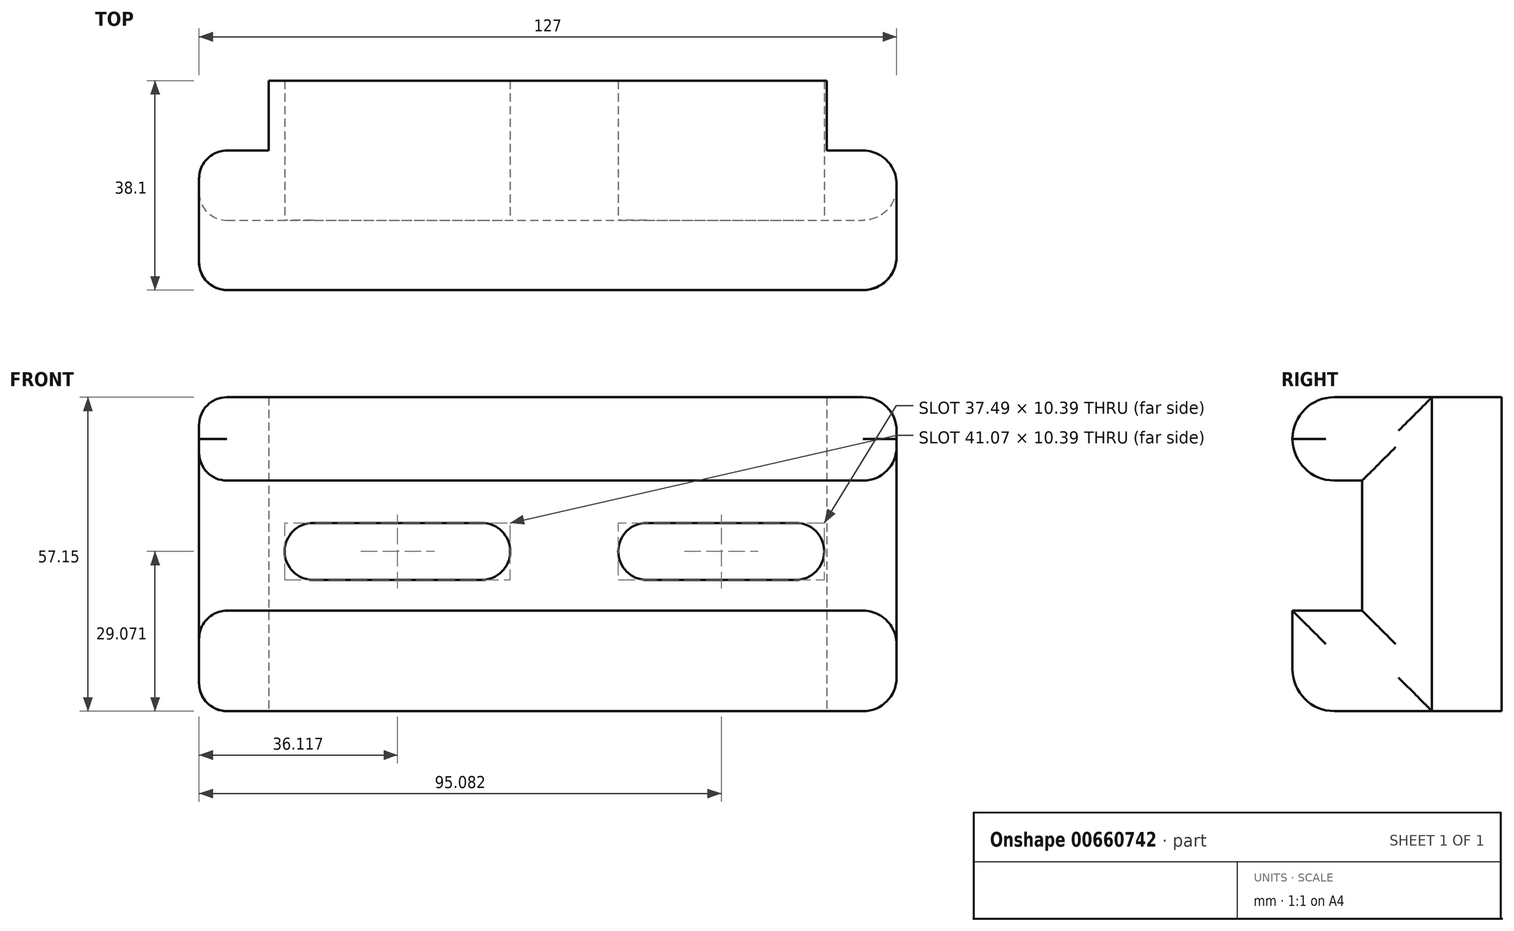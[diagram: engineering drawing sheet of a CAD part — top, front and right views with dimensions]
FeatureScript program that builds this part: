
annotation { "Feature Type Name" : "Feature", "Feature Type Description" : "" }
export const myFeature = defineFeature(function(context is Context, id is Id, definition is map)
    precondition{}
    {
        {
            var Q0;
            Q0=qCreatedBy(makeId("Front.planeOp"),FACE);
            var sketch = newSketch(context, id + "F0", { "sketchPlane" : qUnion([Q0])});
            skLineSegment(sketch, "E0", {"start": v(-81.53, -18.29) * mm, "end": v(45.47, -18.29) * mm});
            skLineSegment(sketch, "E1", {"start": v(-81.53, -18.29) * mm, "end": v(-81.53, 38.86) * mm});
            skLineSegment(sketch, "E2", {"start": v(45.47, -18.29) * mm, "end": v(45.47, 38.86) * mm});
            skLineSegment(sketch, "E3", {"start": v(45.47, 38.86) * mm, "end": v(-81.53, 38.86) * mm});
            skSolve(sketch);
        }
        {
            var Q0;
            Q0=makeQuery(id+"F0.imprint","IMPRINT",FACE,{"disambiguationData":[TD([[makeQuery(id+"F0.imprint","IMPRINT",EDGE,{"derivedFrom":sQuery(id+"F0.wireOp",EDGE,"E0")}),1.0]])]});
            extrude(context, id + "F1", {"entities" : qUnion([Q0]), "depth" : 38.1 * mm, "offsetDistance" : 25.4 * mm});
        }
        {
            var Q0;
            Q0=makeQuery(id+"F1.opExtrude","SWEPT_FACE",FACE,{"disambiguationData":[OSD([sQuery(id+"F0.wireOp",EDGE,"E0")])]});
            var sketch = newSketch(context, id + "F2", { "sketchPlane" : qUnion([Q0])});
            skLineSegment(sketch, "E4", {"start": v(45.47, 12.7) * mm, "end": v(32.77, 12.7) * mm});
            skLineSegment(sketch, "E5", {"start": v(32.77, 12.7) * mm, "end": v(32.77, 0) * mm});
            skLineSegment(sketch, "E6", {"start": v(-81.53, 12.7) * mm, "end": v(-68.83, 12.7) * mm});
            skLineSegment(sketch, "E7", {"start": v(-68.83, 12.7) * mm, "end": v(-68.83, 0) * mm});
            skSolve(sketch);
        }
        {
            var Q0;
            {var subQ0=sQuery(id+"F2.wireOp",EDGE,"E4");Q0=makeQuery(id+"F2.imprint","IMPRINT",FACE,{"disambiguationData":[TD([[makeQuery(id+"F2.imprint","IMPRINT",EDGE,{"derivedFrom":subQ0}),1.0]])]});}
            extrude(context, id + "F3", {"entities" : qUnion([Q0]), "operationType" : NewBodyOperationType.REMOVE, "oppositeDirection" : true, "depth" : 57.15 * mm, "offsetDistance" : 25.4 * mm});
        }
        {
            var Q0;
            {var subQ0=sQuery(id+"F2.wireOp",EDGE,"E6");Q0=makeQuery(id+"F2.imprint","IMPRINT",FACE,{"disambiguationData":[TD([[makeQuery(id+"F2.imprint","IMPRINT",EDGE,{"derivedFrom":subQ0}),-1.0]])]});}
            extrude(context, id + "F4", {"entities" : qUnion([Q0]), "operationType" : NewBodyOperationType.REMOVE, "oppositeDirection" : true, "depth" : 57.15 * mm, "offsetDistance" : 25.4 * mm});
        }
        {
            var Q0;
            Q0=makeQuery(id+"F1.opExtrude","CAP_FACE",FACE,{"disambiguationData":[OSD([sQuery(id+"F0.wireOp",EDGE,"E0"),sQuery(id+"F0.wireOp",EDGE,"E1"),sQuery(id+"F0.wireOp",EDGE,"E2"),sQuery(id+"F0.wireOp",EDGE,"E3")])],"isStart":false});
            var sketch = newSketch(context, id + "F5", { "sketchPlane" : qUnion([Q0])});
            skLineSegment(sketch, "E8", {"start": v(-81.53, 0) * mm, "end": v(45.47, 0) * mm});
            skLineSegment(sketch, "E9", {"start": v(-81.53, 23.68) * mm, "end": v(45.47, 23.68) * mm});
            skSolve(sketch);
        }
        {
            var Q0;
            {var subQ0=sQuery(id+"F5.wireOp",EDGE,"E8");Q0=makeQuery(id+"F5.imprint","IMPRINT",FACE,{"disambiguationData":[TD([[makeQuery(id+"F5.imprint","IMPRINT",EDGE,{"derivedFrom":subQ0}),1.0]])]});}
            extrude(context, id + "F6", {"entities" : qUnion([Q0]), "operationType" : NewBodyOperationType.REMOVE, "oppositeDirection" : true, "depth" : 12.7 * mm, "offsetDistance" : 25.4 * mm});
        }
        {
            var Q0;
            Q0=makeQuery(id+"F1.opExtrude","CAP_EDGE",EDGE,{"disambiguationData":[OSD([sQuery(id+"F0.wireOp",EDGE,"E3")])],"isStart":false});
            var Q1;
            Q1=makeQuery(id+"F6.boolean.opBoolean","COPY",EDGE,{"derivedFrom":makeQuery(id+"F6.opExtrude","CAP_EDGE",EDGE,{"disambiguationData":[OSD([sQuery(id+"F5.wireOp",EDGE,"E9")])],"isStart":true})});
            fillet(context, id + "F7", {"entities" : qUnion([Q0, Q1]), "radius" : 7.62 * mm, "tangentPropagation" : true, "allowEdgeOverflow" : false});
        }
        {
            var Q0;
            Q0=makeQuery(id+"F1.opExtrude","SWEPT_FACE",FACE,{"disambiguationData":[OSD([sQuery(id+"F0.wireOp",EDGE,"E1")])]});
            fillet(context, id + "F8", {"entities" : qUnion([Q0]), "radius" : 5.08 * mm, "tangentPropagation" : true, "allowEdgeOverflow" : false});
        }
        {
            var Q0;
            Q0=makeQuery(id+"F1.opExtrude","CAP_EDGE",EDGE,{"disambiguationData":[OSD([sQuery(id+"F0.wireOp",EDGE,"E0")])],"isStart":false});
            var Q1;
            Q1=makeQuery(id+"F6.boolean.opBoolean","COPY",EDGE,{"derivedFrom":makeQuery(id+"F6.opExtrude","CAP_EDGE",EDGE,{"disambiguationData":[OSD([sQuery(id+"F5.wireOp",EDGE,"E8")])],"isStart":true})});
            fillet(context, id + "F9", {"entities" : qUnion([Q0, Q1]), "radius" : 7.62 * mm, "tangentPropagation" : true, "allowEdgeOverflow" : false});
        }
        {
            var Q0;
            Q0=makeQuery(id+"F1.opExtrude","SWEPT_FACE",FACE,{"disambiguationData":[OSD([sQuery(id+"F0.wireOp",EDGE,"E2")])]});
            fillet(context, id + "F10", {"entities" : qUnion([Q0]), "radius" : 6.1 * mm, "tangentPropagation" : true, "allowEdgeOverflow" : false});
        }
        {
            var Q0;
            Q0=makeQuery(id+"F6.boolean.opBoolean","COPY",FACE,{"derivedFrom":makeQuery(id+"F6.opExtrude","CAP_FACE",FACE,{"disambiguationData":[OSD([sQuery(id+"F0.wireOp",EDGE,"E1"),sQuery(id+"F0.wireOp",EDGE,"E2"),sQuery(id+"F5.wireOp",EDGE,"E8"),sQuery(id+"F5.wireOp",EDGE,"E9")])],"isStart":false})});
            var sketch = newSketch(context, id + "F11", { "sketchPlane" : qUnion([Q0])});
            skCircle(sketch, "E10", {"center": v(-60.75, 10.78) * mm, "radius": 5.2 * mm});
            skCircle(sketch, "E11", {"center": v(-30.07, 10.78) * mm, "radius": 5.2 * mm});
            skCircle(sketch, "E12", {"center": v(0, 10.78) * mm, "radius": 5.2 * mm});
            skCircle(sketch, "E13", {"center": v(27.1, 10.78) * mm, "radius": 5.2 * mm});
            skLineSegment(sketch, "E14", {"start": v(-60.75, 15.98) * mm, "end": v(-30.07, 15.98) * mm});
            skLineSegment(sketch, "E15", {"start": v(-60.75, 5.59) * mm, "end": v(-30.07, 5.59) * mm});
            skLineSegment(sketch, "E16", {"start": v(0, 15.98) * mm, "end": v(27.1, 15.98) * mm});
            skLineSegment(sketch, "E17", {"start": v(0, 5.59) * mm, "end": v(27.1, 5.59) * mm});
            skSolve(sketch);
        }
        {
            var Q0;
            {var subQ0=sQuery(id+"F11.wireOp",EDGE,"E13");var subQ1=makeQuery(id+"F11.imprint","INTERSECT",VERTEX,{"derivedFrom":[subQ0,sQuery(id+"F11.wireOp",EDGE,"E16")]});Q0=makeQuery(id+"F11.imprint","IMPRINT",FACE,{"disambiguationData":[TD([[makeQuery(id+"F11.imprint","IMPRINT",EDGE,{"disambiguationData":[TD([[subQ1,-1.0]])],"derivedFrom":subQ0}),1.0]])]});}
            var Q1;
            {var subQ0=sQuery(id+"F11.wireOp",EDGE,"E16");Q1=makeQuery(id+"F11.imprint","IMPRINT",FACE,{"disambiguationData":[TD([[makeQuery(id+"F11.imprint","IMPRINT",EDGE,{"derivedFrom":subQ0}),-1.0]])]});}
            var Q2;
            {var subQ0=sQuery(id+"F11.wireOp",EDGE,"E12");var subQ1=makeQuery(id+"F11.imprint","INTERSECT",VERTEX,{"derivedFrom":[subQ0,sQuery(id+"F11.wireOp",EDGE,"E16")]});Q2=makeQuery(id+"F11.imprint","IMPRINT",FACE,{"disambiguationData":[TD([[makeQuery(id+"F11.imprint","IMPRINT",EDGE,{"disambiguationData":[TD([[subQ1,-1.0]])],"derivedFrom":subQ0}),1.0]])]});}
            extrude(context, id + "F12", {"entities" : qUnion([Q0, Q1, Q2]), "operationType" : NewBodyOperationType.REMOVE, "oppositeDirection" : true, "depth" : 25.4 * mm, "offsetDistance" : 25.4 * mm});
        }
        {
            var Q0;
            {var subQ0=sQuery(id+"F11.wireOp",EDGE,"E14");Q0=makeQuery(id+"F11.imprint","IMPRINT",FACE,{"disambiguationData":[TD([[makeQuery(id+"F11.imprint","IMPRINT",EDGE,{"derivedFrom":subQ0}),-1.0]])]});}
            var Q1;
            {var subQ0=sQuery(id+"F11.wireOp",EDGE,"E11");var subQ1=makeQuery(id+"F11.imprint","INTERSECT",VERTEX,{"derivedFrom":[subQ0,sQuery(id+"F11.wireOp",EDGE,"E14")]});Q1=makeQuery(id+"F11.imprint","IMPRINT",FACE,{"disambiguationData":[TD([[makeQuery(id+"F11.imprint","IMPRINT",EDGE,{"disambiguationData":[TD([[subQ1,-1.0]])],"derivedFrom":subQ0}),1.0]])]});}
            var Q2;
            {var subQ0=sQuery(id+"F11.wireOp",EDGE,"E10");var subQ1=makeQuery(id+"F11.imprint","INTERSECT",VERTEX,{"derivedFrom":[subQ0,sQuery(id+"F11.wireOp",EDGE,"E14")]});Q2=makeQuery(id+"F11.imprint","IMPRINT",FACE,{"disambiguationData":[TD([[makeQuery(id+"F11.imprint","IMPRINT",EDGE,{"disambiguationData":[TD([[subQ1,-1.0]])],"derivedFrom":subQ0}),1.0]])]});}
            extrude(context, id + "F13", {"entities" : qUnion([Q0, Q1, Q2]), "operationType" : NewBodyOperationType.REMOVE, "oppositeDirection" : true, "depth" : 25.4 * mm, "offsetDistance" : 25.4 * mm});
        }
    });
